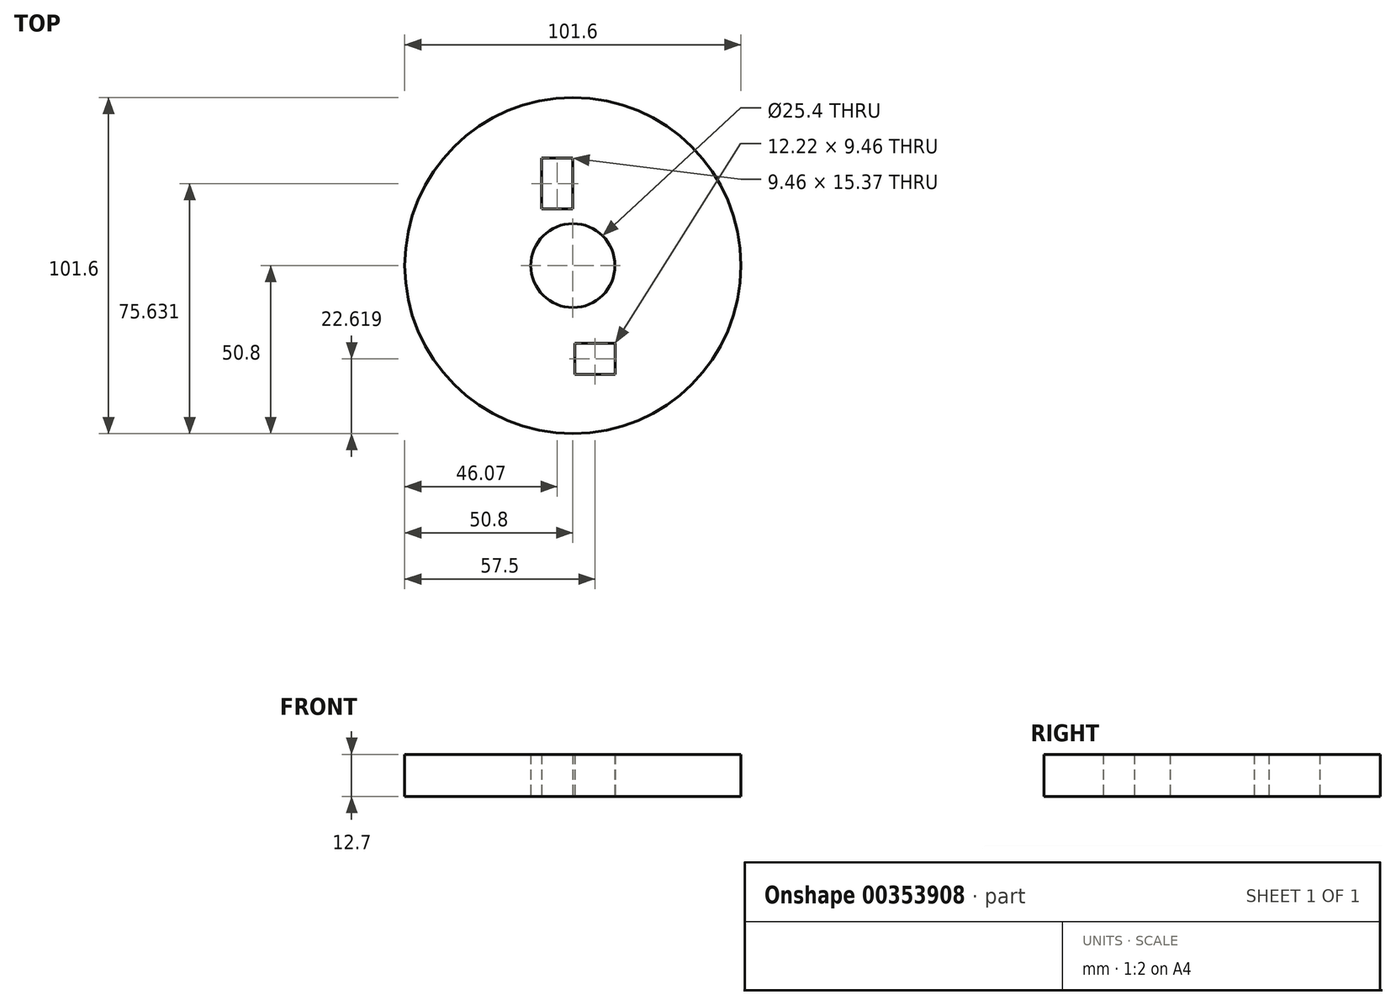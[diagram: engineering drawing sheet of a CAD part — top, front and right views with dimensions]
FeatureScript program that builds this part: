
annotation { "Feature Type Name" : "Feature", "Feature Type Description" : "" }
export const myFeature = defineFeature(function(context is Context, id is Id, definition is map)
    precondition{}
    {
        {
            var Q0;
            Q0=qCreatedBy(makeId("Top.planeOp"),FACE);
            var sketch = newSketch(context, id + "F0", { "sketchPlane" : qUnion([Q0])});
            skCircle(sketch, "E0", {"center": v(0, 0) * mm, "radius": 50.8 * mm});
            skCircle(sketch, "E1", {"center": v(0, 0) * mm, "radius": 12.7 * mm});
            skLineSegment(sketch, "E2.bottom", {"start": v(0, 32.52) * mm, "end": v(-9.46, 32.52) * mm});
            skLineSegment(sketch, "E2.top", {"start": v(0, 17.15) * mm, "end": v(-9.46, 17.15) * mm});
            skLineSegment(sketch, "E2.left", {"start": v(0, 32.52) * mm, "end": v(0, 17.15) * mm});
            skLineSegment(sketch, "E2.right", {"start": v(-9.46, 32.52) * mm, "end": v(-9.46, 17.15) * mm});
            skPoint(sketch, "E2.middle", {"position": v(-4.73, 24.83) * mm});
            skLineSegment(sketch, "E3.bottom", {"start": v(12.8, -32.91) * mm, "end": v(0.6, -32.91) * mm});
            skLineSegment(sketch, "E3.top", {"start": v(12.8, -23.45) * mm, "end": v(0.6, -23.45) * mm});
            skLineSegment(sketch, "E3.left", {"start": v(12.8, -32.91) * mm, "end": v(12.8, -23.45) * mm});
            skLineSegment(sketch, "E3.right", {"start": v(0.6, -32.91) * mm, "end": v(0.6, -23.45) * mm});
            skPoint(sketch, "E3.middle", {"position": v(6.7, -28.18) * mm});
            skSolve(sketch);
        }
        {
            var Q0;
            Q0 = qSketchRegion(id + "F0", true);
            extrude(context, id + "F1", {"entities" : qUnion([Q0]), "depth" : 12.7 * mm});
        }
    });
